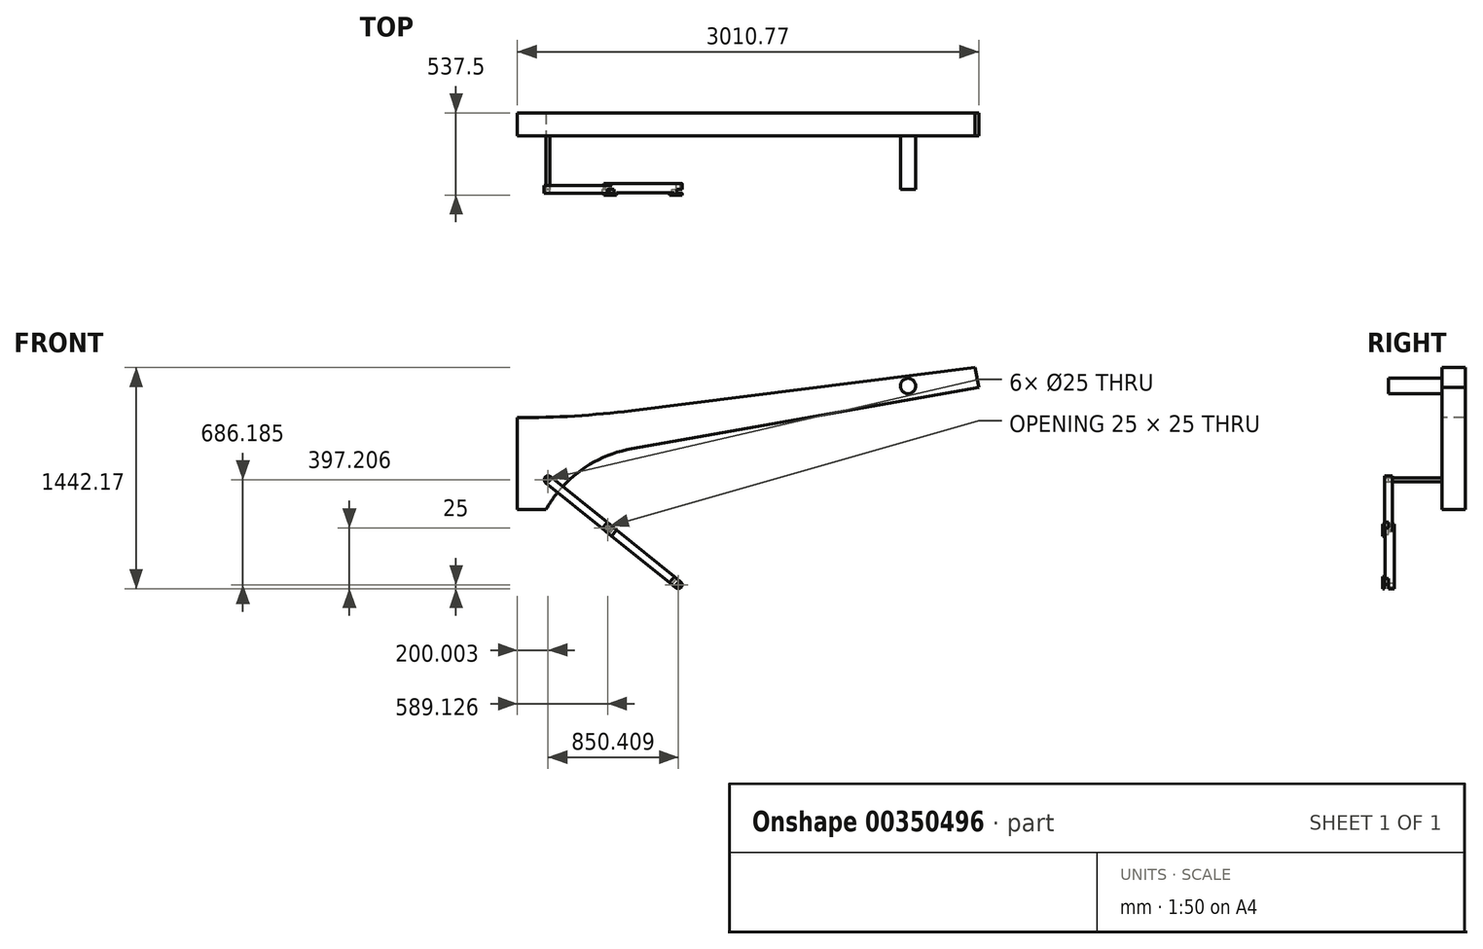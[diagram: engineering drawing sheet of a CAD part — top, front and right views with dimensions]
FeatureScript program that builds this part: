
annotation { "Feature Type Name" : "Feature", "Feature Type Description" : "" }
export const myFeature = defineFeature(function(context is Context, id is Id, definition is map)
    precondition{}
    {
        {
            var Q0;
            Q0=qCreatedBy(makeId("Front.planeOp"),FACE);
            var sketch = newSketch(context, id + "F0", { "sketchPlane" : qUnion([Q0])});
            skLineSegment(sketch, "E0.top", {"start": v(-5, 390) * mm, "end": v(5, 390) * mm});
            skLineSegment(sketch, "E0.left", {"start": v(-155, 170) * mm, "end": v(-155, 240) * mm});
            skLineSegment(sketch, "E0.right", {"start": v(155, 170) * mm, "end": v(155, 240) * mm});
            skPoint(sketch, "E1.visualSharp", {"position": v(-155, 390) * mm});
            skArc(sketch, "E1.filletArc", {"start": v(-5, 390) * mm, "mid": v(-111.07, 346.07) * mm, "end": v(-155, 240) * mm});
            skPoint(sketch, "E2.visualSharp", {"position": v(155, 390) * mm});
            skArc(sketch, "E2.filletArc", {"start": v(155, 240) * mm, "mid": v(111.07, 346.07) * mm, "end": v(5, 390) * mm});
            skLineSegment(sketch, "E3", {"start": v(-130, 75) * mm, "end": v(-105, 75) * mm});
            skLineSegment(sketch, "E4", {"start": v(-105, 75) * mm, "end": v(-105, 30) * mm});
            skLineSegment(sketch, "E5", {"start": v(-105, 30) * mm, "end": v(105, 30) * mm});
            skLineSegment(sketch, "E6", {"start": v(105, 30) * mm, "end": v(105, 150) * mm});
            skLineSegment(sketch, "E7", {"start": v(105, 150) * mm, "end": v(135, 150) * mm});
            skPoint(sketch, "E8.orphan", {"position": v(-155, 0) * mm});
            skPoint(sketch, "E9.visualSharp", {"position": v(155, 150) * mm});
            skArc(sketch, "E9.filletArc", {"start": v(135, 150) * mm, "mid": v(149.14, 155.86) * mm, "end": v(155, 170) * mm});
            skLineSegment(sketch, "E10", {"start": v(-280.75, 0) * mm, "end": v(393.95, 0) * mm});
            skLineSegment(sketch, "E11", {"start": v(-135, 150) * mm, "end": v(-130, 150) * mm});
            skLineSegment(sketch, "E12", {"start": v(-130, 150) * mm, "end": v(-130, 75) * mm});
            skPoint(sketch, "E13.visualSharp", {"position": v(-155, 150) * mm});
            skArc(sketch, "E13.filletArc", {"start": v(-155, 170) * mm, "mid": v(-149.14, 155.86) * mm, "end": v(-135, 150) * mm});
            skSolve(sketch);
        }
        {
            var Q0;
            Q0=qCreatedBy(makeId("Front.planeOp"),FACE);
            var sketch = newSketch(context, id + "F1", { "sketchPlane" : qUnion([Q0])});
            skLineSegment(sketch, "E14", {"start": v(-167, 230.07) * mm, "end": v(-157, 230.07) * mm});
            skLineSegment(sketch, "E15", {"start": v(-157, 230.07) * mm, "end": v(-157, 65) * mm});
            skLineSegment(sketch, "E16", {"start": v(-157, 65) * mm, "end": v(-105, 65) * mm});
            skLineSegment(sketch, "E17", {"start": v(-105, 65) * mm, "end": v(-105, 30) * mm});
            skLineSegment(sketch, "E18", {"start": v(-105, 30) * mm, "end": v(100, 30) * mm});
            skLineSegment(sketch, "E19", {"start": v(105, 25) * mm, "end": v(105, 0) * mm});
            skLineSegment(sketch, "E20", {"start": v(105, 0) * mm, "end": v(-167, 0) * mm});
            skLineSegment(sketch, "E21", {"start": v(-167, 0) * mm, "end": v(-167, 230.07) * mm});
            skPoint(sketch, "E22.visualSharp", {"position": v(105, 30) * mm});
            skArc(sketch, "E22.filletArc", {"start": v(105, 25) * mm, "mid": v(103.54, 28.54) * mm, "end": v(100, 30) * mm});
            skSolve(sketch);
        }
        {
            var Q0;
            Q0=qCreatedBy(makeId("Front.planeOp"),FACE);
            var sketch = newSketch(context, id + "F2", { "sketchPlane" : qUnion([Q0])});
            skLineSegment(sketch, "E23", {"start": v(-205, 0) * mm, "end": v(-205, 240) * mm});
            skLineSegment(sketch, "E24", {"start": v(-305, 0) * mm, "end": v(-305, 240) * mm});
            skArc(sketch, "E25", {"start": v(20.62, 438.35) * mm, "mid": v(-137.05, 390.2) * mm, "end": v(-205, 240) * mm});
            skLineSegment(sketch, "E26", {"start": v(-205, 240) * mm, "end": v(-305, 240) * mm, "construction": true});
            skLineSegment(sketch, "E27", {"start": v(20.62, 438.35) * mm, "end": v(22.33, 588.34) * mm, "construction": true});
            skArc(sketch, "E28", {"start": v(22.33, 588.34) * mm, "mid": v(-210.33, 479) * mm, "end": v(-305, 240) * mm});
            skLineSegment(sketch, "E29", {"start": v(22.33, 588.34) * mm, "end": v(89.49, 592.52) * mm});
            skArc(sketch, "E30", {"start": v(401.06, 544.79) * mm, "mid": v(264.57, 448.23) * mm, "end": v(98.57, 428.28) * mm});
            skArc(sketch, "E31", {"start": v(89.49, 592.52) * mm, "mid": v(177.07, 616.48) * mm, "end": v(247.85, 673.34) * mm});
            skLineSegment(sketch, "E32", {"start": v(247.85, 673.34) * mm, "end": v(401.06, 544.79) * mm, "construction": true});
            skLineSegment(sketch, "E33", {"start": v(324.45, 609.07) * mm, "end": v(1043.85, 1466.41) * mm});
            skLineSegment(sketch, "E34", {"start": v(401.06, 544.79) * mm, "end": v(1128.12, 1395.7) * mm});
            skLineSegment(sketch, "E35", {"start": v(247.85, 673.34) * mm, "end": v(959.59, 1537.12) * mm});
            skLineSegment(sketch, "E36", {"start": v(959.59, 1537.12) * mm, "end": v(1128.12, 1395.7) * mm, "construction": true});
            skArc(sketch, "E37", {"start": v(21.47, 513.35) * mm, "mid": v(-173.83, 434.4) * mm, "end": v(-255, 240) * mm});
            skLineSegment(sketch, "E38", {"start": v(21.47, 513.35) * mm, "end": v(113.82, 512.3) * mm});
            skArc(sketch, "E39", {"start": v(113.82, 512.3) * mm, "mid": v(230, 537.02) * mm, "end": v(324.45, 609.07) * mm});
            skLineSegment(sketch, "E40", {"start": v(20.62, 438.35) * mm, "end": v(98.57, 428.28) * mm});
            skSolve(sketch);
        }
        {
            var Q0;
            Q0=qCreatedBy(makeId("Front.planeOp"),FACE);
            var sketch = newSketch(context, id + "F3", { "sketchPlane" : qUnion([Q0])});
            skLineSegment(sketch, "E41.0", {"start": v(-205, 0) * mm, "end": v(-205, 240) * mm, "construction": true});
            skLineSegment(sketch, "E42.0", {"start": v(-305, 0) * mm, "end": v(-305, 240) * mm, "construction": true});
            skLineSegment(sketch, "E43", {"start": v(-305, 240) * mm, "end": v(-205, 240) * mm, "construction": true});
            skLineSegment(sketch, "E44", {"start": v(-255, 230) * mm, "end": v(-255, 0) * mm, "construction": true});
            skPoint(sketch, "E44.startSnap0", {"position": v(-255, 240) * mm});
            skLineSegment(sketch, "E45", {"start": v(-210, 0) * mm, "end": v(-210, 170) * mm});
            skLineSegment(sketch, "E46", {"start": v(-210, 170) * mm, "end": v(-205, 170) * mm});
            skLineSegment(sketch, "E47", {"start": v(-255, 230) * mm, "end": v(-205, 230) * mm, "construction": true});
            skLineSegment(sketch, "E48", {"start": v(-205, 230) * mm, "end": v(-205, 170) * mm});
            skLineSegment(sketch, "E49", {"start": v(-225, 230) * mm, "end": v(-225, 0.12) * mm});
            skPoint(sketch, "E49.endSnap0", {"position": v(-217.5, 0.12) * mm});
            skLineSegment(sketch, "E50", {"start": v(-225, 230) * mm, "end": v(-205, 230) * mm});
            skLineSegment(sketch, "E51", {"start": v(-210, 0) * mm, "end": v(-210, -170) * mm});
            skLineSegment(sketch, "E52", {"start": v(-225, -200) * mm, "end": v(-240, -200) * mm});
            skLineSegment(sketch, "E53", {"start": v(-225, -100) * mm, "end": v(-225, 0.12) * mm});
            skLineSegment(sketch, "E54", {"start": v(-225, -200) * mm, "end": v(-255, -200) * mm});
            skLineSegment(sketch, "E55", {"start": v(-255, -200) * mm, "end": v(-255, -100) * mm});
            skLineSegment(sketch, "E56", {"start": v(-255, -100) * mm, "end": v(-225, -100) * mm});
            skPoint(sketch, "E57.visualSharp", {"position": v(-210, -200) * mm});
            skArc(sketch, "E57.filletArc", {"start": v(-240, -200) * mm, "mid": v(-218.79, -191.21) * mm, "end": v(-210, -170) * mm});
            skSolve(sketch);
        }
        {
            var Q0;
            Q0=qCreatedBy(makeId("Front.planeOp"),FACE);
            var sketch = newSketch(context, id + "F4", { "sketchPlane" : qUnion([Q0])});
            skPoint(sketch, "E58.0", {"position": v(-167, 115.04) * mm});
            skLineSegment(sketch, "E59.0", {"start": v(-167, 115.04) * mm, "end": v(-167, 200) * mm});
            skPoint(sketch, "E60.orphan", {"position": v(-255, 230) * mm});
            skPoint(sketch, "E61.orphan", {"position": v(-167, 230.07) * mm});
            skLineSegment(sketch, "E62", {"start": v(-167, 200) * mm, "end": v(-367, 0) * mm});
            skLineSegment(sketch, "E63", {"start": v(-367, 0) * mm, "end": v(-197, 0) * mm});
            skLineSegment(sketch, "E64", {"start": v(-167, 130) * mm, "end": v(-197, 100) * mm});
            skLineSegment(sketch, "E65", {"start": v(-197, 100) * mm, "end": v(-197, 0) * mm});
            skPoint(sketch, "E66.orphan", {"position": v(-167, 0) * mm});
            skSolve(sketch);
        }
        {
            var Q0;
            Q0=sQuery(id+"F2.wireOp",EDGE,"E37");
            var Q1;
            Q1=sQuery(id+"F3.wireOp",VERTEX,"E44.startSnap0");
            cPlane(context, id + "F5", {"entities" : qUnion([Q0, Q1]), "cplaneType" : CPlaneType.CURVE_POINT, "offset" : 25 * mm, "width" : 150 * mm, "height" : 150 * mm});
        }
        {
            var Q0;
            Q0=sQuery(id+"F2.wireOp",EDGE,"E37");
            var Q1;
            Q1=sQuery(id+"F2.wireOp",VERTEX,"E37.start");
            cPlane(context, id + "F6", {"entities" : qUnion([Q0, Q1]), "cplaneType" : CPlaneType.CURVE_POINT, "offset" : 25 * mm, "width" : 150 * mm, "height" : 150 * mm});
        }
        {
            var Q0;
            Q0=qCreatedBy(id+"F5.planeOp",FACE);
            var sketch = newSketch(context, id + "F7", { "sketchPlane" : qUnion([Q0])});
            skPoint(sketch, "E67.0", {"position": v(-205, 0) * mm});
            skPoint(sketch, "E68.0", {"position": v(-255, 0) * mm});
            skCircle(sketch, "E69", {"center": v(-255, 0) * mm, "radius": 50 * mm});
            skSolve(sketch);
        }
        {
            var Q0;
            Q0=qCreatedBy(makeId("Front.planeOp"),FACE);
            var sketch = newSketch(context, id + "F8", { "sketchPlane" : qUnion([Q0])});
            skPoint(sketch, "E70.0", {"position": v(-205, 240) * mm});
            skPoint(sketch, "E71.0", {"position": v(20.62, 438.35) * mm});
            skArc(sketch, "E72", {"start": v(20.62, 438.35) * mm, "mid": v(-137.05, 390.2) * mm, "end": v(-205, 240) * mm});
            skPoint(sketch, "E73.0", {"position": v(-305, 240) * mm});
            skPoint(sketch, "E74.0", {"position": v(22.33, 588.34) * mm});
            skArc(sketch, "E75", {"start": v(22.33, 588.34) * mm, "mid": v(-210.33, 479) * mm, "end": v(-305, 240) * mm});
            skSolve(sketch);
        }
        {
            var Q0;
            Q0=qCreatedBy(id+"F6.planeOp",FACE);
            var sketch = newSketch(context, id + "F9", { "sketchPlane" : qUnion([Q0])});
            skPoint(sketch, "E76.0", {"position": v(0, 513.56) * mm});
            skLineSegment(sketch, "E77.bottom", {"start": v(-15, 438.56) * mm, "end": v(15, 438.56) * mm});
            skLineSegment(sketch, "E77.top", {"start": v(-15, 588.56) * mm, "end": v(15, 588.56) * mm});
            skLineSegment(sketch, "E77.left", {"start": v(-65, 488.56) * mm, "end": v(-65, 538.56) * mm});
            skLineSegment(sketch, "E77.right", {"start": v(65, 488.56) * mm, "end": v(65, 538.56) * mm});
            skPoint(sketch, "E78.0", {"position": v(0, 438.56) * mm});
            skPoint(sketch, "E79.visualSharp", {"position": v(65, 588.56) * mm});
            skArc(sketch, "E79.filletArc", {"start": v(65, 538.56) * mm, "mid": v(50.36, 573.91) * mm, "end": v(15, 588.56) * mm});
            skPoint(sketch, "E80.visualSharp", {"position": v(-65, 588.56) * mm});
            skArc(sketch, "E80.filletArc", {"start": v(-15, 588.56) * mm, "mid": v(-50.36, 573.91) * mm, "end": v(-65, 538.56) * mm});
            skPoint(sketch, "E81.visualSharp", {"position": v(-65, 438.56) * mm});
            skArc(sketch, "E81.filletArc", {"start": v(-65, 488.56) * mm, "mid": v(-50.36, 453.2) * mm, "end": v(-15, 438.56) * mm});
            skPoint(sketch, "E82.visualSharp", {"position": v(65, 438.56) * mm});
            skArc(sketch, "E82.filletArc", {"start": v(15, 438.56) * mm, "mid": v(50.36, 453.2) * mm, "end": v(65, 488.56) * mm});
            skSolve(sketch);
        }
        {
            var Q0;
            Q0=qCreatedBy(makeId("Front.planeOp"),FACE);
            var sketch = newSketch(context, id + "F10", { "sketchPlane" : qUnion([Q0])});
            skPoint(sketch, "E83.0", {"position": v(20.62, 438.35) * mm});
            skPoint(sketch, "E84.0", {"position": v(22.33, 588.34) * mm});
            skLineSegment(sketch, "E85", {"start": v(20.62, 438.35) * mm, "end": v(111.11, 426.66) * mm});
            skLineSegment(sketch, "E86", {"start": v(22.33, 588.34) * mm, "end": v(116.4, 594.2) * mm});
            skLineSegment(sketch, "E87", {"start": v(116.4, 594.2) * mm, "end": v(111.11, 426.66) * mm});
            skLineSegment(sketch, "E88", {"start": v(113.76, 510.43) * mm, "end": v(21.47, 513.35) * mm, "construction": true});
            skSolve(sketch);
        }
        {
            var Q0;
            Q0=sQuery(id+"F10.wireOp",EDGE,"E88");
            var Q1;
            Q1=sQuery(id+"F10.wireOp",VERTEX,"E88.start");
            cPlane(context, id + "F11", {"entities" : qUnion([Q0, Q1]), "cplaneType" : CPlaneType.CURVE_POINT, "offset" : 25 * mm, "width" : 150 * mm, "height" : 150 * mm});
        }
        {
            var Q0;
            Q0=qCreatedBy(id+"F11.planeOp",FACE);
            var sketch = newSketch(context, id + "F12", { "sketchPlane" : qUnion([Q0])});
            skPoint(sketch, "E89.0", {"position": v(0, 513.77) * mm});
            skLineSegment(sketch, "E90.bottom", {"start": v(-25, 429.96) * mm, "end": v(25, 429.96) * mm});
            skLineSegment(sketch, "E90.top", {"start": v(-25, 597.58) * mm, "end": v(25, 597.58) * mm});
            skLineSegment(sketch, "E90.left", {"start": v(-75, 479.96) * mm, "end": v(-75, 547.58) * mm});
            skLineSegment(sketch, "E90.right", {"start": v(75, 479.96) * mm, "end": v(75, 547.58) * mm});
            skPoint(sketch, "E91.0", {"position": v(0, 597.58) * mm});
            skPoint(sketch, "E92.0", {"position": v(0, 429.96) * mm});
            skPoint(sketch, "E93.visualSharp", {"position": v(75, 429.96) * mm});
            skArc(sketch, "E93.filletArc", {"start": v(25, 429.96) * mm, "mid": v(60.36, 444.6) * mm, "end": v(75, 479.96) * mm});
            skPoint(sketch, "E94.visualSharp", {"position": v(75, 597.58) * mm});
            skArc(sketch, "E94.filletArc", {"start": v(75, 547.58) * mm, "mid": v(60.36, 582.93) * mm, "end": v(25, 597.58) * mm});
            skPoint(sketch, "E95.visualSharp", {"position": v(-75, 597.58) * mm});
            skArc(sketch, "E95.filletArc", {"start": v(-25, 597.58) * mm, "mid": v(-60.36, 582.93) * mm, "end": v(-75, 547.58) * mm});
            skPoint(sketch, "E96.visualSharp", {"position": v(-75, 429.96) * mm});
            skArc(sketch, "E96.filletArc", {"start": v(-75, 479.96) * mm, "mid": v(-60.36, 444.6) * mm, "end": v(-25, 429.96) * mm});
            skSolve(sketch);
        }
        {
            var Q0;
            Q0=qCreatedBy(makeId("Front.planeOp"),FACE);
            var sketch = newSketch(context, id + "F13", { "sketchPlane" : qUnion([Q0])});
            skPoint(sketch, "E97.0", {"position": v(111.11, 426.66) * mm});
            skPoint(sketch, "E98.0", {"position": v(116.4, 594.2) * mm});
            skArc(sketch, "E99", {"start": v(111.11, 426.66) * mm, "mid": v(273.33, 446.39) * mm, "end": v(406.34, 541.32) * mm});
            skArc(sketch, "E100", {"start": v(116.4, 594.2) * mm, "mid": v(193.48, 615.48) * mm, "end": v(255.46, 666) * mm});
            skLineSegment(sketch, "E101", {"start": v(406.34, 541.32) * mm, "end": v(255.46, 666) * mm});
            skLineSegment(sketch, "E102", {"start": v(330.9, 603.66) * mm, "end": v(1043.85, 1466.41) * mm, "construction": true});
            skLineSegment(sketch, "E103", {"start": v(406.34, 541.32) * mm, "end": v(1128.12, 1395.7) * mm, "construction": true});
            skLineSegment(sketch, "E104", {"start": v(255.46, 666) * mm, "end": v(959.59, 1537.12) * mm, "construction": true});
            skPoint(sketch, "E105.0", {"position": v(113.76, 510.43) * mm});
            skArc(sketch, "E106", {"start": v(113.76, 510.43) * mm, "mid": v(233.6, 530.78) * mm, "end": v(330.9, 603.66) * mm, "construction": true});
            skSolve(sketch);
        }
        {
            var Q0;
            Q0=sQuery(id+"F13.wireOp",EDGE,"E101");
            cPoint(context, id + "F14", {"entities" : qUnion([Q0]), "parameter" : 0.5});
        }
        {
            var Q0;
            Q0=sQuery(id+"F13.wireOp",EDGE,"E106");
            var Q1;
            Q1=qCreatedBy(id+"F14",VERTEX);
            cPlane(context, id + "F15", {"entities" : qUnion([Q0, Q1]), "cplaneType" : CPlaneType.CURVE_POINT, "offset" : 25 * mm, "width" : 150 * mm, "height" : 150 * mm});
        }
        {
            var Q0;
            Q0=qCreatedBy(id+"F15.planeOp",FACE);
            var sketch = newSketch(context, id + "F16", { "sketchPlane" : qUnion([Q0])});
            skPoint(sketch, "E107.0", {"position": v(-129.46, 0) * mm});
            skPoint(sketch, "E108.0", {"position": v(-31.6, 0) * mm});
            skLineSegment(sketch, "E109.bottom", {"start": v(-81.6, 100) * mm, "end": v(-177.32, 100) * mm});
            skLineSegment(sketch, "E109.top", {"start": v(-81.6, -100) * mm, "end": v(-177.32, -100) * mm});
            skLineSegment(sketch, "E109.left", {"start": v(-31.6, 50) * mm, "end": v(-31.6, -50) * mm});
            skLineSegment(sketch, "E109.right", {"start": v(-227.32, 50) * mm, "end": v(-227.32, -50) * mm});
            skPoint(sketch, "E110.visualSharp", {"position": v(-31.6, -100) * mm});
            skArc(sketch, "E110.filletArc", {"start": v(-81.6, -100) * mm, "mid": v(-46.25, -85.36) * mm, "end": v(-31.6, -50) * mm});
            skPoint(sketch, "E111.visualSharp", {"position": v(-227.32, -100) * mm});
            skArc(sketch, "E111.filletArc", {"start": v(-227.32, -50) * mm, "mid": v(-212.68, -85.36) * mm, "end": v(-177.32, -100) * mm});
            skPoint(sketch, "E112.visualSharp", {"position": v(-227.32, 100) * mm});
            skArc(sketch, "E112.filletArc", {"start": v(-177.32, 100) * mm, "mid": v(-212.68, 85.36) * mm, "end": v(-227.32, 50) * mm});
            skPoint(sketch, "E113.visualSharp", {"position": v(-31.6, 100) * mm});
            skArc(sketch, "E113.filletArc", {"start": v(-31.6, 50) * mm, "mid": v(-46.25, 85.36) * mm, "end": v(-81.6, 100) * mm});
            skSolve(sketch);
        }
        {
            var Q0;
            Q0=sQuery(id+"F13.wireOp",EDGE,"E102");
            var Q1;
            Q1=sQuery(id+"F13.wireOp",VERTEX,"E102.end");
            cPlane(context, id + "F17", {"entities" : qUnion([Q0, Q1]), "cplaneType" : CPlaneType.CURVE_POINT, "offset" : 25 * mm, "width" : 150 * mm, "height" : 150 * mm});
        }
        {
            var Q0;
            Q0=qCreatedBy(id+"F17.planeOp",FACE);
            var sketch = newSketch(context, id + "F18", { "sketchPlane" : qUnion([Q0])});
            skPoint(sketch, "E114.0", {"position": v(-129.46, 0) * mm});
            skPoint(sketch, "E115.0", {"position": v(-19.47, 0) * mm});
            skLineSegment(sketch, "E116.bottom", {"start": v(-69.47, 200) * mm, "end": v(-189.46, 200) * mm});
            skLineSegment(sketch, "E116.top", {"start": v(-69.47, -200) * mm, "end": v(-189.46, -200) * mm});
            skLineSegment(sketch, "E116.left", {"start": v(-19.47, 150) * mm, "end": v(-19.47, -150) * mm});
            skLineSegment(sketch, "E116.right", {"start": v(-239.46, 150) * mm, "end": v(-239.46, -150) * mm});
            skPoint(sketch, "E117.visualSharp", {"position": v(-239.46, -200) * mm});
            skArc(sketch, "E117.filletArc", {"start": v(-239.46, -150) * mm, "mid": v(-224.81, -185.36) * mm, "end": v(-189.46, -200) * mm});
            skPoint(sketch, "E118.visualSharp", {"position": v(-239.46, 200) * mm});
            skArc(sketch, "E118.filletArc", {"start": v(-189.46, 200) * mm, "mid": v(-224.81, 185.36) * mm, "end": v(-239.46, 150) * mm});
            skPoint(sketch, "E119.visualSharp", {"position": v(-19.47, 200) * mm});
            skArc(sketch, "E119.filletArc", {"start": v(-19.47, 150) * mm, "mid": v(-34.11, 185.36) * mm, "end": v(-69.47, 200) * mm});
            skPoint(sketch, "E120.visualSharp", {"position": v(-19.47, -200) * mm});
            skArc(sketch, "E120.filletArc", {"start": v(-69.47, -200) * mm, "mid": v(-34.11, -185.36) * mm, "end": v(-19.47, -150) * mm});
            skSolve(sketch);
        }
        {
            var Q0;
            Q0=qCreatedBy(makeId("Front.planeOp"),FACE);
            var sketch = newSketch(context, id + "F19", { "sketchPlane" : qUnion([Q0])});
            skPoint(sketch, "E121.0", {"position": v(-255, 240) * mm});
            skPoint(sketch, "E122.0", {"position": v(-225, -100) * mm});
            skLineSegment(sketch, "E123.bottom", {"start": v(-255, 240) * mm, "end": v(-225, 240) * mm});
            skLineSegment(sketch, "E123.top", {"start": v(-255, -100) * mm, "end": v(-225, -100) * mm});
            skLineSegment(sketch, "E123.left", {"start": v(-255, 240) * mm, "end": v(-255, -100) * mm});
            skLineSegment(sketch, "E123.right", {"start": v(-225, 240) * mm, "end": v(-225, -100) * mm});
            skSolve(sketch);
        }
        {
            var Q0;
            Q0=qCreatedBy(makeId("Front.planeOp"),FACE);
            var sketch = newSketch(context, id + "F20", { "sketchPlane" : qUnion([Q0])});
            skPoint(sketch, "E124.0", {"position": v(-255, 240) * mm});
            skArc(sketch, "E125", {"start": v(-250.39, 290) * mm, "mid": v(-253.84, 265.1) * mm, "end": v(-255, 240) * mm});
            skLineSegment(sketch, "E126", {"start": v(-255, 240) * mm, "end": v(-375.39, 240) * mm});
            skLineSegment(sketch, "E127", {"start": v(-400.39, 265) * mm, "end": v(-400.39, 265) * mm});
            skLineSegment(sketch, "E128", {"start": v(-375.39, 290) * mm, "end": v(-250.39, 290) * mm});
            skPoint(sketch, "E129.visualSharp", {"position": v(-400.39, 290) * mm});
            skArc(sketch, "E129.filletArc", {"start": v(-375.39, 290) * mm, "mid": v(-393.07, 282.68) * mm, "end": v(-400.39, 265) * mm});
            skPoint(sketch, "E130.visualSharp", {"position": v(-400.39, 240) * mm});
            skArc(sketch, "E130.filletArc", {"start": v(-400.39, 265) * mm, "mid": v(-393.07, 247.32) * mm, "end": v(-375.39, 240) * mm});
            skCircle(sketch, "E131", {"center": v(-375.39, 265) * mm, "radius": 12.5 * mm});
            skSolve(sketch);
        }
        {
            var Q0;
            Q0=qCreatedBy(makeId("Front.planeOp"),FACE);
            var sketch = newSketch(context, id + "F21", { "sketchPlane" : qUnion([Q0])});
            skLineSegment(sketch, "E132.0", {"start": v(959.59, 1537.12) * mm, "end": v(1128.12, 1395.7) * mm});
            skLineSegment(sketch, "E133", {"start": v(986.4, 1514.62) * mm, "end": v(1066.75, 1610.38) * mm});
            skLineSegment(sketch, "E134", {"start": v(1172.41, 1619.62) * mm, "end": v(1172.41, 1619.62) * mm});
            skLineSegment(sketch, "E135", {"start": v(1181.66, 1513.96) * mm, "end": v(1101.3, 1418.2) * mm});
            skLineSegment(sketch, "E136", {"start": v(1172.41, 1619.62) * mm, "end": v(1043.85, 1466.41) * mm, "construction": true});
            skPoint(sketch, "E137.visualSharp", {"position": v(1114.96, 1667.83) * mm});
            skArc(sketch, "E137.filletArc", {"start": v(1172.41, 1619.62) * mm, "mid": v(1117.67, 1636.88) * mm, "end": v(1066.75, 1610.38) * mm});
            skPoint(sketch, "E138.visualSharp", {"position": v(1229.87, 1571.41) * mm});
            skArc(sketch, "E138.filletArc", {"start": v(1181.66, 1513.96) * mm, "mid": v(1198.92, 1568.7) * mm, "end": v(1172.41, 1619.62) * mm});
            skCircle(sketch, "E139", {"center": v(1124.2, 1562.17) * mm, "radius": 50 * mm});
            skSolve(sketch);
        }
        {
            var Q0;
            Q0=qCreatedBy(makeId("Front.planeOp"),FACE);
            var sketch = newSketch(context, id + "F22", { "sketchPlane" : qUnion([Q0])});
            skPoint(sketch, "E140.0", {"position": v(1124.2, 1562.17) * mm});
            skPoint(sketch, "E141.0", {"position": v(-5, 390) * mm});
            skLineSegment(sketch, "E142", {"start": v(-5, 390) * mm, "end": v(0, 0) * mm, "construction": true});
            skLineSegment(sketch, "E143", {"start": v(0, 0) * mm, "end": v(0, -390.03) * mm, "construction": true});
            skLineSegment(sketch, "E144", {"start": v(0, -390.03) * mm, "end": v(0, -590.03) * mm, "construction": true});
            skCircle(sketch, "E145", {"center": v(1124.2, 1562.17) * mm, "radius": 2428.13 * mm, "construction": true});
            skLineSegment(sketch, "E146", {"start": v(1124.2, 1562.17) * mm, "end": v(0, 0) * mm, "construction": true});
            skLineSegment(sketch, "E147", {"start": v(1124.2, 1562.17) * mm, "end": v(-771.19, 1227.96) * mm, "construction": true});
            skLineSegment(sketch, "E148", {"start": v(-771.19, 1227.96) * mm, "end": v(-1182.98, 805.4) * mm, "construction": true});
            skLineSegment(sketch, "E149", {"start": v(-771.19, 1227.96) * mm, "end": v(-631.6, 1371.2) * mm, "construction": true});
            skCircle(sketch, "E150", {"center": v(-1425.8, 1555) * mm, "radius": 900 * mm, "construction": true});
            skLineSegment(sketch, "E151", {"start": v(-875.88, 1120.53) * mm, "end": v(-732.64, 980.95) * mm, "construction": true});
            skLineSegment(sketch, "E152", {"start": v(-1425.8, 1555) * mm, "end": v(-1225.8, 951.19) * mm, "construction": true});
            skLineSegment(sketch, "E153", {"start": v(-1225.8, 951.19) * mm, "end": v(-1625.8, 951.19) * mm, "construction": true});
            skLineSegment(sketch, "E154", {"start": v(-1625.8, 951.19) * mm, "end": v(-1425.8, 1555) * mm, "construction": true});
            skLineSegment(sketch, "E155", {"start": v(-1425.8, 1555) * mm, "end": v(-1425.8, 951.19) * mm, "construction": true});
            skPoint(sketch, "E156.0", {"position": v(-375.39, 265) * mm});
            skLineSegment(sketch, "E157", {"start": v(0, 0) * mm, "end": v(-375.39, 265) * mm, "construction": true});
            skLineSegment(sketch, "E158", {"start": v(-771.19, 1227.96) * mm, "end": v(-855.1, 1679.74) * mm, "construction": true});
            skLineSegment(sketch, "E159", {"start": v(-1225.8, 951.19) * mm, "end": v(-836.67, 637.2) * mm, "construction": true});
            skLineSegment(sketch, "E160", {"start": v(-836.67, 637.2) * mm, "end": v(-375.39, 265) * mm, "construction": true});
            skLineSegment(sketch, "E161", {"start": v(-1225.8, 951.19) * mm, "end": v(-1389.61, 1423.59) * mm, "construction": true});
            skLineSegment(sketch, "E162", {"start": v(-1389.61, 1423.59) * mm, "end": v(-855.1, 1679.74) * mm, "construction": true});
            skSolve(sketch);
        }
        {
            var Q0;
            Q0=qCreatedBy(makeId("Front.planeOp"),FACE);
            var sketch = newSketch(context, id + "F23", { "sketchPlane" : qUnion([Q0])});
            skPoint(sketch, "E163.0", {"position": v(-375.39, 265) * mm});
            skPoint(sketch, "E164.0", {"position": v(-375.39, 240) * mm});
            skArc(sketch, "E165", {"start": v(-391.09, 245.54) * mm, "mid": v(-355.93, 249.3) * mm, "end": v(-359.69, 284.46) * mm});
            skLineSegment(sketch, "E166", {"start": v(-359.69, 284.46) * mm, "end": v(-820.98, 656.66) * mm});
            skArc(sketch, "E167", {"start": v(-820.98, 656.66) * mm, "mid": v(-856.13, 652.9) * mm, "end": v(-852.37, 617.75) * mm});
            skLineSegment(sketch, "E168", {"start": v(-852.37, 617.75) * mm, "end": v(-391.09, 245.54) * mm});
            skCircle(sketch, "E169.0", {"center": v(-375.39, 265) * mm, "radius": 12.5 * mm});
            skCircle(sketch, "E170", {"center": v(-836.67, 637.2) * mm, "radius": 12.5 * mm});
            skSolve(sketch);
        }
        {
            var Q0;
            Q0=qCreatedBy(makeId("Front.planeOp"),FACE);
            var sketch = newSketch(context, id + "F24", { "sketchPlane" : qUnion([Q0])});
            skPoint(sketch, "E171.0", {"position": v(-836.67, 637.2) * mm});
            skPoint(sketch, "E172.0", {"position": v(-820.98, 656.66) * mm});
            skArc(sketch, "E173", {"start": v(-852.37, 617.75) * mm, "mid": v(-817.22, 621.5) * mm, "end": v(-820.98, 656.66) * mm});
            skPoint(sketch, "E174.0", {"position": v(-1225.8, 951.19) * mm});
            skArc(sketch, "E175", {"start": v(-1210.1, 970.64) * mm, "mid": v(-1245.25, 966.88) * mm, "end": v(-1241.5, 931.73) * mm});
            skLineSegment(sketch, "E176", {"start": v(-1210.1, 970.64) * mm, "end": v(-820.98, 656.66) * mm});
            skLineSegment(sketch, "E177", {"start": v(-1241.5, 931.73) * mm, "end": v(-852.37, 617.75) * mm});
            skCircle(sketch, "E178.0", {"center": v(-836.67, 637.2) * mm, "radius": 12.5 * mm});
            skCircle(sketch, "E179", {"center": v(-1225.8, 951.19) * mm, "radius": 12.5 * mm});
            skSolve(sketch);
        }
        {
            var Q0;
            Q0=makeQuery(id+"F23.imprint","IMPRINT",FACE,{"disambiguationData":[TD([[makeQuery(id+"F23.imprint","IMPRINT",EDGE,{"derivedFrom":sQuery(id+"F23.wireOp",EDGE,"E165")}),1.0]])]});
            extrude(context, id + "F25", {"entities" : qUnion([Q0]), "endBound" : BoundingType.SYMMETRIC, "depth" : 75 * mm});
        }
        {
            var Q0;
            Q0=makeQuery(id+"F24.imprint","IMPRINT",FACE,{"disambiguationData":[TD([[makeQuery(id+"F24.imprint","IMPRINT",EDGE,{"derivedFrom":sQuery(id+"F24.wireOp",EDGE,"E173")}),1.0]])]});
            extrude(context, id + "F26", {"entities" : qUnion([Q0]), "endBound" : BoundingType.SYMMETRIC, "depth" : 50 * mm});
        }
        {
            var Q0;
            Q0=makeQuery(id+"F25.opExtrude","SWEPT_FACE",FACE,{"disambiguationData":[OSD([sQuery(id+"F23.wireOp",EDGE,"E166")])]});
            var sketch = newSketch(context, id + "F27", { "sketchPlane" : qUnion([Q0])});
            skLineSegment(sketch, "E180", {"start": v(-996.28, -37.5) * mm, "end": v(-996.28, -22.5) * mm});
            skLineSegment(sketch, "E181", {"start": v(-996.28, -22.5) * mm, "end": v(-513.55, -22.5) * mm});
            skLineSegment(sketch, "E182", {"start": v(-513.55, -22.5) * mm, "end": v(-513.55, -37.5) * mm});
            skLineSegment(sketch, "E183", {"start": v(-754.92, -22.5) * mm, "end": v(-754.92, -37.5) * mm, "construction": true});
            skPoint(sketch, "E184.0", {"position": v(-1026.28, -25) * mm});
            skLineSegment(sketch, "E185", {"start": v(-1026.28, -25) * mm, "end": v(-1051.28, -25) * mm});
            skLineSegment(sketch, "E186", {"start": v(-1026.28, -25) * mm, "end": v(-1016.28, -25) * mm});
            skLineSegment(sketch, "E187", {"start": v(-1016.28, -25) * mm, "end": v(-1016.28, 0) * mm});
            skLineSegment(sketch, "E188", {"start": v(-1016.28, 0) * mm, "end": v(-1051.28, 0) * mm});
            skLineSegment(sketch, "E189", {"start": v(-1051.28, 0) * mm, "end": v(-1051.28, -25) * mm, "construction": true});
            skLineSegment(sketch, "E190", {"start": v(-458.55, -25) * mm, "end": v(-493.55, -25) * mm});
            skLineSegment(sketch, "E191", {"start": v(-493.55, -25) * mm, "end": v(-493.55, 0) * mm});
            skLineSegment(sketch, "E192", {"start": v(-493.55, 0) * mm, "end": v(-458.55, 0) * mm});
            skLineSegment(sketch, "E193", {"start": v(-458.55, 0) * mm, "end": v(-458.55, -25) * mm, "construction": true});
            skLineSegment(sketch, "E194", {"start": v(-1076.28, -25) * mm, "end": v(-1076.28, 0) * mm});
            skLineSegment(sketch, "E195", {"start": v(-1051.28, -25) * mm, "end": v(-1076.28, -25) * mm});
            skLineSegment(sketch, "E196", {"start": v(-1051.28, 0) * mm, "end": v(-1076.28, 0) * mm});
            skPoint(sketch, "E197.orphan", {"position": v(-1076.28, -37.5) * mm});
            skPoint(sketch, "E198.orphan", {"position": v(-1076.28, 37.5) * mm});
            skLineSegment(sketch, "E199", {"start": v(-433.55, 0) * mm, "end": v(-433.55, -25) * mm});
            skLineSegment(sketch, "E200", {"start": v(-458.55, -25) * mm, "end": v(-433.55, -25) * mm});
            skLineSegment(sketch, "E201", {"start": v(-458.55, 0) * mm, "end": v(-433.55, 0) * mm});
            skPoint(sketch, "E202.orphan", {"position": v(-433.55, -37.5) * mm});
            skPoint(sketch, "E203.orphan", {"position": v(-433.55, 37.5) * mm});
            skSolve(sketch);
        }
        {
            var Q0;
            Q0=makeQuery(id+"F27.imprint","IMPRINT",FACE,{"disambiguationData":[TD([[makeQuery(id+"F27.imprint","IMPRINT",EDGE,{"derivedFrom":sQuery(id+"F27.wireOp",EDGE,"E199")}),-1.0]])]});
            var Q1;
            {var subQ0=sQuery(id+"F27.wireOp",EDGE,"E190");Q1=makeQuery(id+"F27.imprint","IMPRINT",FACE,{"disambiguationData":[TD([[makeQuery(id+"F27.imprint","IMPRINT",EDGE,{"derivedFrom":subQ0}),-1.0]])]});}
            var Q2;
            {var subQ0=sQuery(id+"F27.wireOp",EDGE,"E180");Q2=makeQuery(id+"F27.imprint","IMPRINT",FACE,{"disambiguationData":[TD([[makeQuery(id+"F27.imprint","IMPRINT",EDGE,{"derivedFrom":subQ0}),-1.0]])]});}
            var Q3;
            {var subQ1=sQuery(id+"F27.wireOp",EDGE,"E185");Q3=makeQuery(id+"F27.imprint","IMPRINT",FACE,{"disambiguationData":[TD([[makeQuery(id+"F27.imprint","IMPRINT",EDGE,{"derivedFrom":subQ1}),-1.0]])]});}
            var Q4;
            Q4=makeQuery(id+"F27.imprint","IMPRINT",FACE,{"disambiguationData":[TD([[makeQuery(id+"F27.imprint","IMPRINT",EDGE,{"derivedFrom":sQuery(id+"F27.wireOp",EDGE,"E194")}),-1.0]])]});
            extrude(context, id + "F28", {"entities" : qUnion([Q0, Q1, Q2, Q3, Q4]), "operationType" : NewBodyOperationType.REMOVE, "endBound" : BoundingType.THROUGH_ALL, "oppositeDirection" : true, "depth" : 25 * mm});
        }
        {
            var Q0;
            Q0=qCreatedBy(makeId("Front.planeOp"),FACE);
            var sketch = newSketch(context, id + "F29", { "sketchPlane" : qUnion([Q0])});
            skCircle(sketch, "E204.0", {"center": v(-1225.8, 951.19) * mm, "radius": 12.5 * mm});
            skCircle(sketch, "E205.0", {"center": v(1124.2, 1562.17) * mm, "radius": 50 * mm});
            skSolve(sketch);
        }
        {
            var Q0;
            Q0=makeQuery(id+"F21.imprint","IMPRINT",FACE,{"disambiguationData":[TD([[makeQuery(id+"F21.imprint","IMPRINT",EDGE,{"derivedFrom":sQuery(id+"F21.wireOp",EDGE,"E139")}),1.0]])]});
            var Q1;
            Q1=makeQuery(id+"F29.imprint","IMPRINT",FACE,{"disambiguationData":[TD([[makeQuery(id+"F29.imprint","IMPRINT",EDGE,{"derivedFrom":sQuery(id+"F29.wireOp",EDGE,"E204.0")}),1.0]])]});
            extrude(context, id + "F30", {"entities" : qUnion([Q0, Q1]), "oppositeDirection" : true, "depth" : 350 * mm});
        }
        {
            var Q0;
            Q0=makeQuery(id+"F30.opExtrude","CAP_FACE",FACE,{"disambiguationData":[OSD([sQuery(id+"F21.wireOp",EDGE,"E139")])],"isStart":false});
            var sketch = newSketch(context, id + "F31", { "sketchPlane" : qUnion([Q0])});
            skPoint(sketch, "E206.0", {"position": v(1425.8, 1555) * mm});
            skLineSegment(sketch, "E207", {"start": v(1425.8, 1555) * mm, "end": v(1425.8, 755) * mm, "construction": true});
            skLineSegment(sketch, "E208", {"start": v(1425.8, 755) * mm, "end": v(1239.63, 755) * mm});
            skArc(sketch, "E209", {"start": v(1239.63, 755) * mm, "mid": v(1004.7, 1016.96) * mm, "end": v(680.09, 1152.78) * mm});
            skLineSegment(sketch, "E210", {"start": v(680.09, 1152.78) * mm, "end": v(-1584.97, 1552.17) * mm});
            skLineSegment(sketch, "E211", {"start": v(-1584.97, 1552.17) * mm, "end": v(-1562.05, 1682.17) * mm});
            skLineSegment(sketch, "E212", {"start": v(-1562.05, 1682.17) * mm, "end": v(680.6, 1401.46) * mm});
            skArc(sketch, "E213", {"start": v(680.6, 1401.46) * mm, "mid": v(1052.47, 1366.63) * mm, "end": v(1425.8, 1355) * mm});
            skLineSegment(sketch, "E214", {"start": v(1425.8, 1355) * mm, "end": v(1425.8, 755) * mm});
            skSolve(sketch);
        }
        {
            var Q0;
            Q0=makeQuery(id+"F31.imprint","IMPRINT",FACE,{"disambiguationData":[TD([[makeQuery(id+"F31.imprint","IMPRINT",EDGE,{"derivedFrom":makeQuery(id+"F30.opExtrude","CAP_EDGE",EDGE,{"disambiguationData":[OSD([sQuery(id+"F21.wireOp",EDGE,"E139")])],"isStart":false})}),-1.0]])]});
            var Q1;
            Q1=makeQuery(id+"F31.imprint","IMPRINT",FACE,{"disambiguationData":[TD([[makeQuery(id+"F31.imprint","IMPRINT",EDGE,{"derivedFrom":sQuery(id+"F31.wireOp",EDGE,"E208")}),-1.0]])]});
            extrude(context, id + "F32", {"entities" : qUnion([Q0, Q1]), "operationType" : NewBodyOperationType.ADD, "depth" : 150 * mm});
        }
    });
